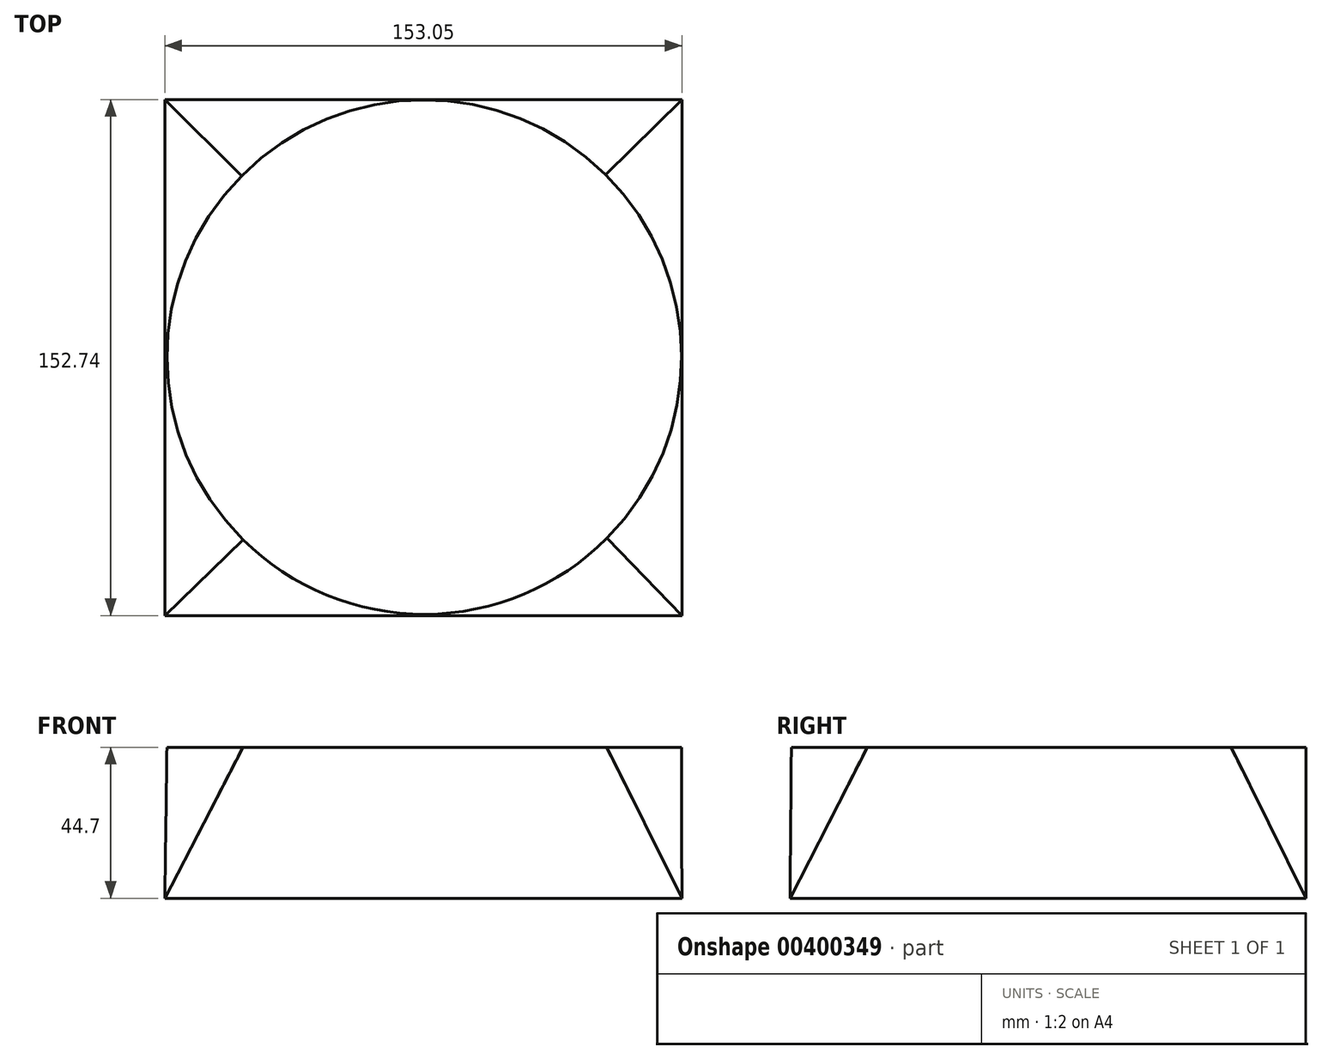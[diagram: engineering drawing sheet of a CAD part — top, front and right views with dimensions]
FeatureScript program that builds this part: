
annotation { "Feature Type Name" : "Feature", "Feature Type Description" : "" }
export const myFeature = defineFeature(function(context is Context, id is Id, definition is map)
    precondition{}
    {
        {
            var Q0;
            Q0=qCreatedBy(makeId("Top.planeOp"),FACE);
            cPlane(context, id + "F0", {"entities" : qUnion([Q0]), "cplaneType" : CPlaneType.OFFSET, "offset" : 44.7 * mm, "width" : 152.4 * mm, "height" : 152.4 * mm});
        }
        {
            var Q0;
            Q0=qCreatedBy(id+"F0.planeOp",FACE);
            var sketch = newSketch(context, id + "F1", { "sketchPlane" : qUnion([Q0])});
            skCircle(sketch, "E0", {"center": v(0, 0) * mm, "radius": 76.13 * mm});
            skSolve(sketch);
        }
        {
            var Q0;
            Q0=qCreatedBy(makeId("Top.planeOp"),FACE);
            var sketch = newSketch(context, id + "F2", { "sketchPlane" : qUnion([Q0])});
            skLineSegment(sketch, "E1.bottom", {"start": v(-76.79, 76.22) * mm, "end": v(76.26, 76.22) * mm});
            skLineSegment(sketch, "E1.top", {"start": v(-76.79, -76.52) * mm, "end": v(76.26, -76.52) * mm});
            skLineSegment(sketch, "E1.left", {"start": v(-76.79, 76.22) * mm, "end": v(-76.79, -76.52) * mm});
            skLineSegment(sketch, "E1.right", {"start": v(76.26, 76.22) * mm, "end": v(76.26, -76.52) * mm});
            skSolve(sketch);
        }
        {
            var Q0;
            Q0 = qSketchRegion(id + "F1", true);
            var Q1;
            Q1 = qSketchRegion(id + "F2", true);
            loft(context, id + "F3", {"sheetProfilesArray" : [{ "sheetProfileEntities" : qUnion([Q0]) }, { "sheetProfileEntities" : qUnion([Q1]) }]});
        }
    });
